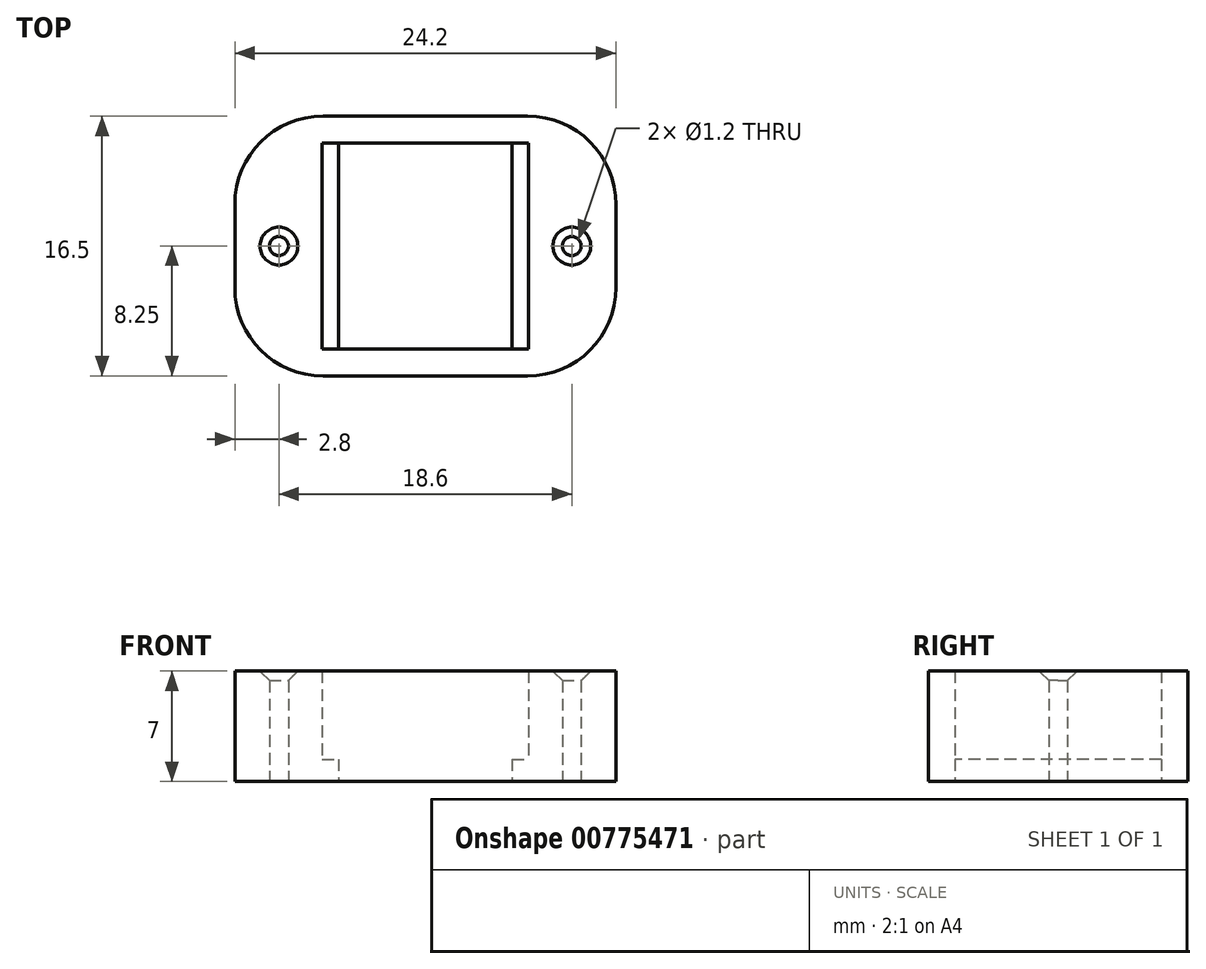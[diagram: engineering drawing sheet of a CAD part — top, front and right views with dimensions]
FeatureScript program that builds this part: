
annotation { "Feature Type Name" : "Feature", "Feature Type Description" : "" }
export const myFeature = defineFeature(function(context is Context, id is Id, definition is map)
    precondition{}
    {
        {
            var Q0;
            Q0=qCreatedBy(makeId("Top.planeOp"),FACE);
            var sketch = newSketch(context, id + "F0", { "sketchPlane" : qUnion([Q0])});
            skLineSegment(sketch, "E0.bottom", {"start": v(12.1, 8.25) * mm, "end": v(-12.1, 8.25) * mm});
            skLineSegment(sketch, "E0.top", {"start": v(12.1, -8.25) * mm, "end": v(-12.1, -8.25) * mm});
            skLineSegment(sketch, "E0.left", {"start": v(12.1, 8.25) * mm, "end": v(12.1, -8.25) * mm});
            skLineSegment(sketch, "E0.right", {"start": v(-12.1, 8.25) * mm, "end": v(-12.1, -8.25) * mm});
            skPoint(sketch, "E0.middle", {"position": v(0, 0) * mm});
            skSolve(sketch);
        }
        {
            var Q0;
            Q0=makeQuery(id+"F0.imprint","IMPRINT",FACE,{"disambiguationData":[TD([[makeQuery(id+"F0.imprint","IMPRINT",EDGE,{"derivedFrom":sQuery(id+"F0.wireOp",EDGE,"E0.bottom")}),1.0]])]});
            extrude(context, id + "F1", {"entities" : qUnion([Q0]), "depth" : (1.5 + 1.6 + 2.5 + 1.4) * mm, "offsetDistance" : 25 * mm});
        }
        {
            var Q0;
            Q0=makeQuery(id+"F1.opExtrude","SWEPT_EDGE",EDGE,{"disambiguationData":[OSD([sQuery(id+"F0.wireOp",EDGE,"E0.top"),sQuery(id+"F0.wireOp",EDGE,"E0.right")])]});
            var Q1;
            Q1=makeQuery(id+"F1.opExtrude","SWEPT_EDGE",EDGE,{"disambiguationData":[OSD([sQuery(id+"F0.wireOp",EDGE,"E0.top"),sQuery(id+"F0.wireOp",EDGE,"E0.left")])]});
            var Q2;
            Q2=makeQuery(id+"F1.opExtrude","SWEPT_EDGE",EDGE,{"disambiguationData":[OSD([sQuery(id+"F0.wireOp",EDGE,"E0.bottom"),sQuery(id+"F0.wireOp",EDGE,"E0.left")])]});
            var Q3;
            Q3=makeQuery(id+"F1.opExtrude","SWEPT_EDGE",EDGE,{"disambiguationData":[OSD([sQuery(id+"F0.wireOp",EDGE,"E0.bottom"),sQuery(id+"F0.wireOp",EDGE,"E0.right")])]});
            fillet(context, id + "F2", {"entities" : qUnion([Q0, Q1, Q2, Q3]), "radius" : 5.6 * mm, "tangentPropagation" : true, "allowEdgeOverflow" : false});
        }
        {
            var Q0;
            Q0=makeQuery(id+"F1.opExtrude","CAP_FACE",FACE,{"disambiguationData":[OSD([sQuery(id+"F0.wireOp",EDGE,"E0.bottom"),sQuery(id+"F0.wireOp",EDGE,"E0.top"),sQuery(id+"F0.wireOp",EDGE,"E0.left"),sQuery(id+"F0.wireOp",EDGE,"E0.right")])],"isStart":true});
            var sketch = newSketch(context, id + "F3", { "sketchPlane" : qUnion([Q0])});
            skLineSegment(sketch, "E1.bottom", {"start": v(-6.55, -6.55) * mm, "end": v(6.55, -6.55) * mm});
            skLineSegment(sketch, "E1.top", {"start": v(-6.55, 6.55) * mm, "end": v(6.55, 6.55) * mm});
            skLineSegment(sketch, "E1.left", {"start": v(-6.55, -6.55) * mm, "end": v(-6.55, 6.55) * mm});
            skLineSegment(sketch, "E1.right", {"start": v(6.55, -6.55) * mm, "end": v(6.55, 6.55) * mm});
            skPoint(sketch, "E1.middle", {"position": v(0, 0) * mm});
            skSolve(sketch);
        }
        {
            var Q0;
            Q0=qSketchRegion(id+"F3",true);
            extrude(context, id + "F4", {"entities" : qUnion([Q0]), "operationType" : NewBodyOperationType.REMOVE, "endBound" : BoundingType.THROUGH_ALL, "oppositeDirection" : true, "depth" : 25 * mm, "offsetDistance" : 25 * mm});
        }
        {
            var Q0;
            Q0=makeQuery(id+"F1.opExtrude","CAP_FACE",FACE,{"disambiguationData":[OSD([sQuery(id+"F0.wireOp",EDGE,"E0.bottom"),sQuery(id+"F0.wireOp",EDGE,"E0.top"),sQuery(id+"F0.wireOp",EDGE,"E0.left"),sQuery(id+"F0.wireOp",EDGE,"E0.right")])],"isStart":true});
            var sketch = newSketch(context, id + "F5", { "sketchPlane" : qUnion([Q0])});
            skLineSegment(sketch, "E2", {"start": v(-6.55, 6.55) * mm, "end": v(-5.5, 6.55) * mm, "construction": true});
            skLineSegment(sketch, "E3", {"start": v(0, 6.55) * mm, "end": v(0, -6.55) * mm, "construction": true});
            skLineSegment(sketch, "E4.bottom", {"start": v(-5.5, 6.55) * mm, "end": v(-6.55, 6.55) * mm});
            skLineSegment(sketch, "E4.top", {"start": v(-5.5, -6.55) * mm, "end": v(-6.55, -6.55) * mm});
            skLineSegment(sketch, "E4.left", {"start": v(-5.5, 6.55) * mm, "end": v(-5.5, -6.55) * mm});
            skLineSegment(sketch, "E4.right", {"start": v(-6.55, 6.55) * mm, "end": v(-6.55, -6.55) * mm});
            skLineSegment(sketch, "E5.MirrorCS", {"start": v(5.5, 6.55) * mm, "end": v(6.55, 6.55) * mm});
            skLineSegment(sketch, "E6.MirrorCS", {"start": v(5.5, 6.55) * mm, "end": v(5.5, -6.55) * mm});
            skLineSegment(sketch, "E7.MirrorCS", {"start": v(5.5, -6.55) * mm, "end": v(6.55, -6.55) * mm});
            skLineSegment(sketch, "E8.MirrorCS", {"start": v(6.55, 6.55) * mm, "end": v(6.55, -6.55) * mm});
            skLineSegment(sketch, "E9.MirrorCS", {"start": v(6.55, 6.55) * mm, "end": v(5.5, 6.55) * mm, "construction": true});
            skSolve(sketch);
        }
        {
            var Q0;
            Q0=qSketchRegion(id+"F5",true);
            extrude(context, id + "F6", {"entities" : qUnion([Q0]), "operationType" : NewBodyOperationType.ADD, "oppositeDirection" : true, "depth" : 1.4 * mm, "offsetDistance" : 25 * mm});
        }
        {
            var Q0;
            Q0=makeQuery(id+"F6.boolean.opBoolean","MERGE",FACE,{"derivedFrom":[makeQuery(id+"F1.opExtrude","CAP_FACE",FACE,{"disambiguationData":[OSD([sQuery(id+"F0.wireOp",EDGE,"E0.bottom"),sQuery(id+"F0.wireOp",EDGE,"E0.top"),sQuery(id+"F0.wireOp",EDGE,"E0.left"),sQuery(id+"F0.wireOp",EDGE,"E0.right")])],"isStart":true}),makeQuery(id+"F6.opExtrude","CAP_FACE",FACE,{"disambiguationData":[OSD([sQuery(id+"F5.wireOp",EDGE,"E4.bottom"),sQuery(id+"F5.wireOp",EDGE,"E4.top"),sQuery(id+"F5.wireOp",EDGE,"E4.left"),sQuery(id+"F5.wireOp",EDGE,"E4.right")])],"isStart":true}),makeQuery(id+"F6.opExtrude","CAP_FACE",FACE,{"disambiguationData":[OSD([sQuery(id+"F5.wireOp",EDGE,"E5.MirrorCS"),sQuery(id+"F5.wireOp",EDGE,"E6.MirrorCS"),sQuery(id+"F5.wireOp",EDGE,"E7.MirrorCS"),sQuery(id+"F5.wireOp",EDGE,"E8.MirrorCS")])],"isStart":true})]});
            var sketch = newSketch(context, id + "F7", { "sketchPlane" : qUnion([Q0])});
            skLineSegment(sketch, "E10", {"start": v(0, 6.55) * mm, "end": v(0, -6.55) * mm, "construction": true});
            skLineSegment(sketch, "E11", {"start": v(-12.1, 0) * mm, "end": v(-9.3, 0) * mm, "construction": true});
            skCircle(sketch, "E12", {"center": v(-9.3, 0) * mm, "radius": 0.6 * mm});
            skCircle(sketch, "E13.MirrorC", {"center": v(9.3, 0) * mm, "radius": 0.6 * mm});
            skSolve(sketch);
        }
        {
            var Q0;
            Q0=qSketchRegion(id+"F7",true);
            extrude(context, id + "F8", {"entities" : qUnion([Q0]), "operationType" : NewBodyOperationType.REMOVE, "endBound" : BoundingType.THROUGH_ALL, "oppositeDirection" : true, "depth" : 25 * mm, "offsetDistance" : 25 * mm});
        }
        {
            var Q0;
            Q0=makeQuery(id+"F8.boolean.opBoolean","INTERSECT",EDGE,{"derivedFrom":[makeQuery(id+"F1.opExtrude","CAP_FACE",FACE,{"disambiguationData":[OSD([sQuery(id+"F0.wireOp",EDGE,"E0.bottom"),sQuery(id+"F0.wireOp",EDGE,"E0.top"),sQuery(id+"F0.wireOp",EDGE,"E0.left"),sQuery(id+"F0.wireOp",EDGE,"E0.right")])],"isStart":false}),makeQuery(id+"F8.opExtrude","SWEPT_FACE",FACE,{"disambiguationData":[OSD([sQuery(id+"F7.wireOp",EDGE,"E13.MirrorC")])]})]});
            var Q1;
            Q1=makeQuery(id+"F8.boolean.opBoolean","INTERSECT",EDGE,{"derivedFrom":[makeQuery(id+"F1.opExtrude","CAP_FACE",FACE,{"disambiguationData":[OSD([sQuery(id+"F0.wireOp",EDGE,"E0.bottom"),sQuery(id+"F0.wireOp",EDGE,"E0.top"),sQuery(id+"F0.wireOp",EDGE,"E0.left"),sQuery(id+"F0.wireOp",EDGE,"E0.right")])],"isStart":false}),makeQuery(id+"F8.opExtrude","SWEPT_FACE",FACE,{"disambiguationData":[OSD([sQuery(id+"F7.wireOp",EDGE,"E12")])]})]});
            chamfer(context, id + "F9", {"entities" : qUnion([Q0, Q1]), "width" : .6 * mm, "tangentPropagation" : true});
        }
    });
